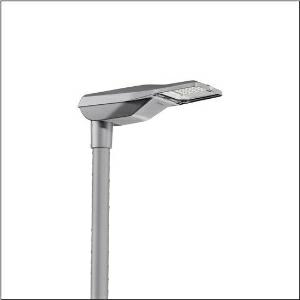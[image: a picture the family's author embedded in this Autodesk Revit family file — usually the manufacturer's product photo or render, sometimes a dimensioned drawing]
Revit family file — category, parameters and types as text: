
# Revit family: streetlight_sl_21_iq_micro___st1_0a_5xe1d21g08cb_51d7
name_source: partatom
category: Lighting Fixtures
units: mm (PartAtom-declared; Revit-internal decimal feet)

## family parameters
Cut with Voids When Loaded = No
Host = Face
Light Source = No
Part Type = Normal
Room Calculation Point = No
Round Connector Dimension = Use Diameter
Shared = No

## types (1)
- --- (1 x LED, 2380 lm, 19.4 W, 2200K)
    Apparent Load = 19 VA
    CIE Flux Codes = 37 72 97 100 100
    Color Rendering = 70
    Color Temperature = 2200K
    Default Elevation = 1800 mm
    Description = Streetlight SL 21 iQ micro, mast luminaire, primary light control with lens, of PMMA, primary optical cover: cover, of toughened safety glass, transparent, light distribution: ST1.0a, light emission: direct distribution, primary light characteristic: asymmetric, installation type: post-top, side-entry, LED, High Power LED, rated luminous flux: 2.380lm, luminous efficacy: 123lm/W, light colour: 722, colour temperature: 2200K, control gear: iQ Street-Remote, control: Street-Remote, Auto-Match, Temp-Guard, Lumen-Switch, Night-Set, Smart-Wire, Light-Fading, Desk-Remote (wireless, voltage-free reading and setting of iQ features in the workshop via application-optimized NFC function/RFID function), optimised constant luminous flux control (CLO 2.0), pre-setting: linear dimming characteristic, mains connection: 220..240V, AC, 50/60Hz, start of lifetime: 19W, end of service life: 20W, reduction: 10W, luminaire housing, of diecast aluminium, powder-coated, Siteco® metallic grey (DB 702S), corrosivity category C5 mid according to DIN EN ISO 12944, please order mast flange separately, inclination adjustable: 0°, 5°, 10°, 15°, sealing non-destructively replaceable, multi-level sealing system, length: 528mm, width: 235mm, height: 110mm, mast flange for spigot size: 42mm (side-entry): 5XC10008XM4, 60/48mm (side-entry/post-top): 5XC10108XM2, 76/60mm (side-entry/post-top): 5XC10108XM1, protection rating (complete): IP66, insulation class (complete): insulation class II (safety insulation), certification: CE, ENEC, ENEC+, VDE, impact resistance: IK10, permissible operating ambient temperature for outdoor applications: -40..+50°C, standard-compliant lighting for roads and squares, packaging unit: 1 piece

Light Distribution: ST1.0a
    Height = 110 mm
    Lamp = 1 x LED
    Lamp Light Flux = 2380 lm
    Lamp Power = 19.4 W
    Lamp count = 1
    Length = 528 mm
    Luminous efficacy = 123 lm/W
    Manufacturer = Siteco
    ModVariant = No
    Model = 5XE1D21G08CB
    Number of Poles = 1
    OnlyDefault = Yes
    Power Factor = 1
    Product Name = Streetlight SL 21 iQ micro | ST1.0a
    Product group = mast luminaire | pylon top
    ProductGroupID = 6100
    Protection Class = Protection class II
    Protection Degree = IP 66
    RLX_Detail_Level = 1
    RLX_Emergency_Light_Flux = 0 lm
    RLX_Emergency_Type = 0
    RLX_Emergency_Type_DB = No
    RlxData = <blob elided: 98645 chars, md5=5cd2a051>
    Socket = socket
    Standby Power = 0 W
    System Light Flux = 2380 lm
    System Power = 19 W
    Type Comments = factory setting: luminous flux: 100 % | dim-lin: 254 | 387 mA
    Type Image = l_1006881.jpg
    URL = http://relux.com
    VarID = @adj_139324
    Voltage = 0 V
    Weight = 0.00 kg
    Width = 235 mm

## geometry (parser evidence)
native form markers: Blend x4, Sweep x11
no freeform markers — native parametric forms only
